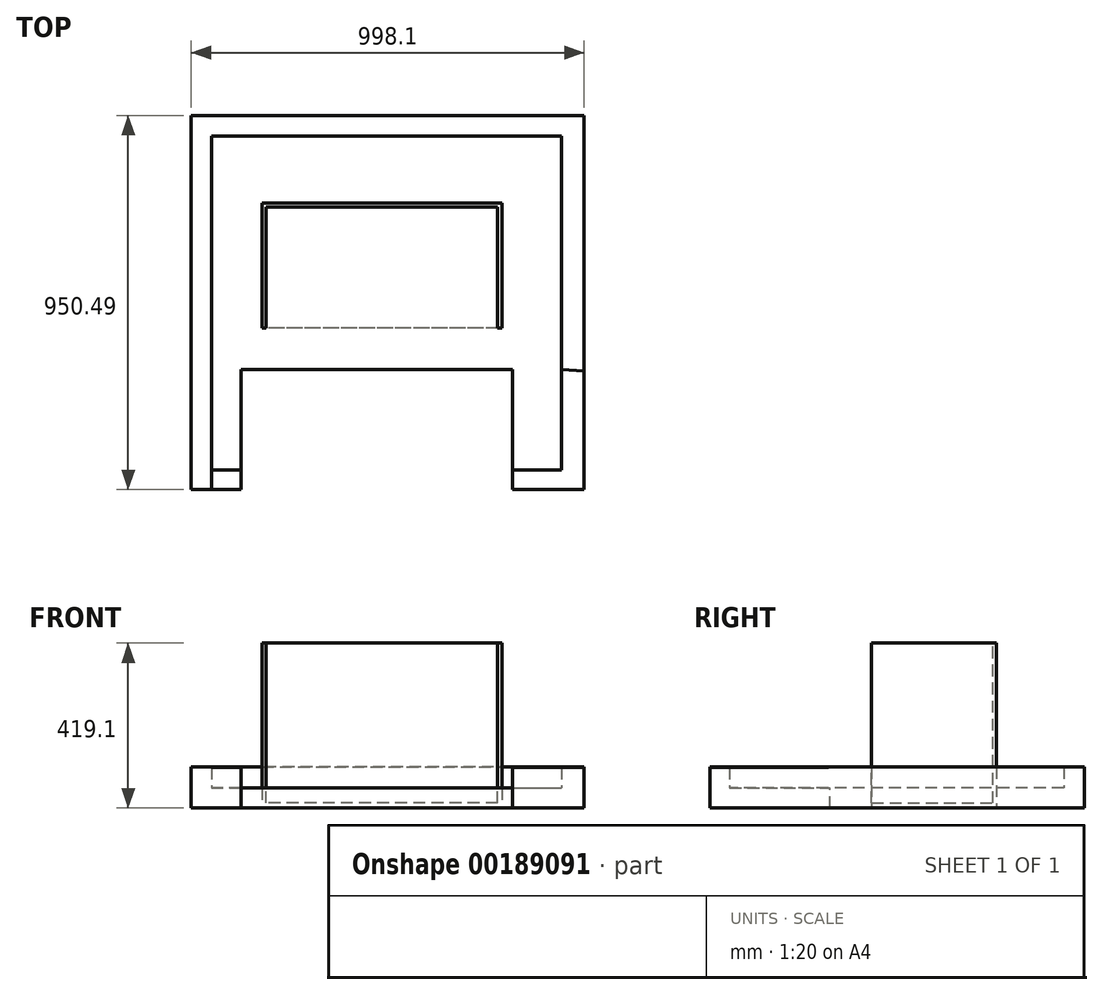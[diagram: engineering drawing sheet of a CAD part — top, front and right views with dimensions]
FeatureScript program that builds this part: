
annotation { "Feature Type Name" : "Feature", "Feature Type Description" : "" }
export const myFeature = defineFeature(function(context is Context, id is Id, definition is map)
    precondition{}
    {
        {
            var Q0;
            Q0=qCreatedBy(makeId("Top.planeOp"),FACE);
            var sketch = newSketch(context, id + "F0", { "sketchPlane" : qUnion([Q0])});
            skLineSegment(sketch, "E0.bottom", {"start": v(0, 0) * mm, "end": v(-609.6, 0) * mm});
            skLineSegment(sketch, "E0.top", {"start": v(0, -317.5) * mm, "end": v(-609.6, -317.5) * mm});
            skLineSegment(sketch, "E0.left", {"start": v(0, 0) * mm, "end": v(0, -317.5) * mm});
            skLineSegment(sketch, "E0.right", {"start": v(-609.6, 0) * mm, "end": v(-609.6, -317.5) * mm});
            skSolve(sketch);
        }
        {
            var Q0;
            Q0=makeQuery(id+"F0.imprint","IMPRINT",FACE,{"disambiguationData":[TD([[makeQuery(id+"F0.imprint","IMPRINT",EDGE,{"derivedFrom":sQuery(id+"F0.wireOp",EDGE,"E0.bottom")}),1.0]])]});
            extrude(context, id + "F1", {"entities" : qUnion([Q0]), "depth" : 419.1 * mm});
        }
        {
            var Q0;
            Q0=makeQuery(id+"F1.opExtrude","CAP_FACE",FACE,{"disambiguationData":[OSD([sQuery(id+"F0.wireOp",EDGE,"E0.bottom"),sQuery(id+"F0.wireOp",EDGE,"E0.top"),sQuery(id+"F0.wireOp",EDGE,"E0.left"),sQuery(id+"F0.wireOp",EDGE,"E0.right")])],"isStart":false});
            var sketch = newSketch(context, id + "F2", { "sketchPlane" : qUnion([Q0])});
            skLineSegment(sketch, "E1.bottom", {"start": v(-599.08, -317.5) * mm, "end": v(-10.7, -317.5) * mm});
            skLineSegment(sketch, "E1.top", {"start": v(-599.08, -9.65) * mm, "end": v(-10.7, -9.65) * mm});
            skLineSegment(sketch, "E1.left", {"start": v(-599.08, -317.5) * mm, "end": v(-599.08, -9.65) * mm});
            skLineSegment(sketch, "E1.right", {"start": v(-10.7, -317.5) * mm, "end": v(-10.7, -9.65) * mm});
            skSolve(sketch);
        }
        {
            var Q0;
            Q0=makeQuery(id+"F2.imprint","IMPRINT",FACE,{"disambiguationData":[TD([[makeQuery(id+"F2.imprint","IMPRINT",EDGE,{"derivedFrom":sQuery(id+"F2.wireOp",EDGE,"E1.bottom")}),-1.0]])]});
            extrude(context, id + "F3", {"entities" : qUnion([Q0]), "operationType" : NewBodyOperationType.REMOVE, "oppositeDirection" : true, "depth" : 406.4 * mm});
        }
        {
            var Q0;
            Q0=qCreatedBy(makeId("Top.planeOp"),FACE);
            var sketch = newSketch(context, id + "F4", { "sketchPlane" : qUnion([Q0])});
            skLineSegment(sketch, "E2.bottom", {"start": v(-737.99, 170.9) * mm, "end": v(151.01, 170.9) * mm});
            skLineSegment(sketch, "E2.top", {"start": v(-737.99, -423.02) * mm, "end": v(151.01, -423.02) * mm});
            skLineSegment(sketch, "E2.left", {"start": v(-737.99, 170.9) * mm, "end": v(-737.99, -423.02) * mm});
            skLineSegment(sketch, "E2.right", {"start": v(151.01, 170.9) * mm, "end": v(151.01, -423.02) * mm});
            skSolve(sketch);
        }
        {
            var Q0;
            Q0=makeQuery(id+"F4.imprint","IMPRINT",FACE,{"disambiguationData":[TD([[makeQuery(id+"F4.imprint","IMPRINT",EDGE,{"derivedFrom":sQuery(id+"F4.wireOp",EDGE,"E2.bottom")}),-1.0]])]});
            extrude(context, id + "F5", {"entities" : qUnion([Q0]), "depth" : 50.8 * mm});
        }
        {
            var Q0;
            Q0=makeQuery(id+"F5.opExtrude","CAP_FACE",FACE,{"disambiguationData":[OSD([sQuery(id+"F4.wireOp",EDGE,"E2.bottom"),sQuery(id+"F4.wireOp",EDGE,"E2.top"),sQuery(id+"F4.wireOp",EDGE,"E2.left"),sQuery(id+"F4.wireOp",EDGE,"E2.right")])],"isStart":true});
            var sketch = newSketch(context, id + "F6", { "sketchPlane" : qUnion([Q0])});
            skLineSegment(sketch, "E3.bottom", {"start": v(-737.99, 423.02) * mm, "end": v(-789.06, 423.02) * mm});
            skLineSegment(sketch, "E3.top", {"start": v(-737.99, -170.9) * mm, "end": v(-789.06, -170.9) * mm});
            skLineSegment(sketch, "E3.left", {"start": v(-737.99, 423.02) * mm, "end": v(-737.99, -170.9) * mm});
            skLineSegment(sketch, "E3.right", {"start": v(-789.06, 423.02) * mm, "end": v(-789.06, -170.9) * mm});
            skLineSegment(sketch, "E4.bottom", {"start": v(-789.06, 423.02) * mm, "end": v(151.01, 423.02) * mm});
            skLineSegment(sketch, "E4.top", {"start": v(-789.06, 500.05) * mm, "end": v(151.01, 500.05) * mm});
            skLineSegment(sketch, "E4.left", {"start": v(-789.06, 423.02) * mm, "end": v(-789.06, 500.05) * mm});
            skLineSegment(sketch, "E4.right", {"start": v(151.01, 423.02) * mm, "end": v(151.01, 500.05) * mm});
            skLineSegment(sketch, "E5.top", {"start": v(151.01, -170.9) * mm, "end": v(209.04, -170.9) * mm});
            skLineSegment(sketch, "E5.left", {"start": v(151.01, 500.05) * mm, "end": v(151.01, -170.9) * mm});
            skLineSegment(sketch, "E5.right", {"start": v(209.04, 426.81) * mm, "end": v(209.04, -170.9) * mm});
            skLineSegment(sketch, "E6.bottom", {"start": v(209.04, -170.9) * mm, "end": v(-789.06, -170.9) * mm});
            skLineSegment(sketch, "E6.top", {"start": v(209.04, -222.67) * mm, "end": v(-789.06, -222.67) * mm});
            skLineSegment(sketch, "E6.left", {"start": v(209.04, -170.9) * mm, "end": v(209.04, -222.67) * mm});
            skLineSegment(sketch, "E6.right", {"start": v(-789.06, -170.9) * mm, "end": v(-789.06, -222.67) * mm});
            skLineSegment(sketch, "E7", {"start": v(151.01, 423.02) * mm, "end": v(209.04, 426.81) * mm});
            skSolve(sketch);
        }
        {
            var Q0;
            {var subQ0=sQuery(id+"F6.wireOp",EDGE,"E3.left");Q0=makeQuery(id+"F6.imprint","IMPRINT",FACE,{"disambiguationData":[TD([[makeQuery(id+"F6.imprint","IMPRINT",EDGE,{"derivedFrom":subQ0}),1.0]])]});}
            var Q1;
            Q1=makeQuery(id+"F6.imprint","IMPRINT",FACE,{"disambiguationData":[TD([[makeQuery(id+"F6.imprint","IMPRINT",EDGE,{"derivedFrom":sQuery(id+"F6.wireOp",EDGE,"E6.top")}),-1.0]])]});
            var Q2;
            {var subQ5=sQuery(id+"F6.wireOp",EDGE,"E5.bottom");Q2=makeQuery(id+"F6.imprint","IMPRINT",FACE,{"disambiguationData":[TD([[makeQuery(id+"F6.imprint","IMPRINT",EDGE,{"derivedFrom":subQ5}),-1.0]])]});}
            var Q3;
            {var subQ4=sQuery(id+"F6.wireOp",EDGE,"E5.right");Q3=makeQuery(id+"F6.imprint","IMPRINT",FACE,{"disambiguationData":[TD([[makeQuery(id+"F6.imprint","IMPRINT",EDGE,{"derivedFrom":subQ4}),-1.0]])]});}
            extrude(context, id + "F7", {"entities" : qUnion([Q0, Q1, Q2, Q3]), "operationType" : NewBodyOperationType.ADD, "oppositeDirection" : true, "depth" : 104.14 * mm});
        }
        {
            var Q0;
            Q0=makeQuery(id+"F7.boolean.opBoolean","MERGE",FACE,{"derivedFrom":[makeQuery(id+"F5.opExtrude","SWEPT_FACE",FACE,{"disambiguationData":[OSD([sQuery(id+"F4.wireOp",EDGE,"E2.top")])]}),makeQuery(id+"F7.opExtrude","SWEPT_FACE",FACE,{"disambiguationData":[OSD([sQuery(id+"F6.wireOp",EDGE,"E4.bottom")])]})]});
            var sketch = newSketch(context, id + "F8", { "sketchPlane" : qUnion([Q0])});
            skLineSegment(sketch, "E8.bottom", {"start": v(-789.06, 0) * mm, "end": v(-662.47, 0) * mm});
            skLineSegment(sketch, "E8.top", {"start": v(-789.06, 50.8) * mm, "end": v(-662.47, 50.8) * mm});
            skLineSegment(sketch, "E8.left", {"start": v(-789.06, 0) * mm, "end": v(-789.06, 50.8) * mm});
            skLineSegment(sketch, "E8.right", {"start": v(-662.47, 0) * mm, "end": v(-662.47, 50.8) * mm});
            skLineSegment(sketch, "E9.bottom", {"start": v(-789.06, 104.14) * mm, "end": v(-737.99, 104.14) * mm});
            skLineSegment(sketch, "E9.top", {"start": v(-789.06, 50.8) * mm, "end": v(-737.99, 50.8) * mm});
            skLineSegment(sketch, "E9.left", {"start": v(-789.06, 104.14) * mm, "end": v(-789.06, 50.8) * mm});
            skLineSegment(sketch, "E9.right", {"start": v(-737.99, 104.14) * mm, "end": v(-737.99, 50.8) * mm});
            skLineSegment(sketch, "E10.bottom", {"start": v(151.01, 0) * mm, "end": v(27.1, 0) * mm});
            skLineSegment(sketch, "E10.top", {"start": v(151.01, 50.8) * mm, "end": v(27.1, 50.8) * mm});
            skLineSegment(sketch, "E10.left", {"start": v(151.01, 0) * mm, "end": v(151.01, 50.8) * mm});
            skLineSegment(sketch, "E10.right", {"start": v(27.1, 0) * mm, "end": v(27.1, 50.8) * mm});
            skLineSegment(sketch, "E11.bottom", {"start": v(151.01, 0) * mm, "end": v(209.04, 0) * mm});
            skLineSegment(sketch, "E11.top", {"start": v(151.01, 103.33) * mm, "end": v(209.04, 103.33) * mm});
            skLineSegment(sketch, "E11.left", {"start": v(151.01, 0) * mm, "end": v(151.01, 103.33) * mm});
            skLineSegment(sketch, "E11.right", {"start": v(209.04, 0) * mm, "end": v(209.04, 103.33) * mm});
            skSolve(sketch);
        }
        {
            var Q0;
            Q0 = qSketchRegion(id + "F8", true);
            extrude(context, id + "F9", {"entities" : qUnion([Q0]), "operationType" : NewBodyOperationType.ADD, "depth" : 304.8 * mm});
        }
        {
            var Q0;
            Q0=makeQuery(id+"F9.boolean.opBoolean","MERGE",FACE,{"derivedFrom":[makeQuery(id+"F5.opExtrude","CAP_FACE",FACE,{"disambiguationData":[OSD([sQuery(id+"F4.wireOp",EDGE,"E2.bottom"),sQuery(id+"F4.wireOp",EDGE,"E2.top"),sQuery(id+"F4.wireOp",EDGE,"E2.left"),sQuery(id+"F4.wireOp",EDGE,"E2.right")])],"isStart":false}),makeQuery(id+"F9.opExtrude","SWEPT_FACE",FACE,{"disambiguationData":[OSD([sQuery(id+"F8.wireOp",EDGE,"E8.top")])]}),makeQuery(id+"F9.opExtrude","SWEPT_FACE",FACE,{"disambiguationData":[OSD([sQuery(id+"F8.wireOp",EDGE,"E10.top")])]})]});
            var sketch = newSketch(context, id + "F10", { "sketchPlane" : qUnion([Q0])});
            skLineSegment(sketch, "E12.bottom", {"start": v(-662.47, -727.82) * mm, "end": v(-737.99, -727.82) * mm});
            skLineSegment(sketch, "E12.top", {"start": v(-662.47, -678.34) * mm, "end": v(-737.99, -678.34) * mm});
            skLineSegment(sketch, "E12.left", {"start": v(-662.47, -727.82) * mm, "end": v(-662.47, -678.34) * mm});
            skLineSegment(sketch, "E12.right", {"start": v(-737.99, -727.82) * mm, "end": v(-737.99, -678.34) * mm});
            skLineSegment(sketch, "E13.bottom", {"start": v(27.1, -727.82) * mm, "end": v(151.01, -727.82) * mm});
            skLineSegment(sketch, "E13.top", {"start": v(27.1, -678.34) * mm, "end": v(151.01, -678.34) * mm});
            skLineSegment(sketch, "E13.left", {"start": v(27.1, -727.82) * mm, "end": v(27.1, -678.34) * mm});
            skLineSegment(sketch, "E13.right", {"start": v(151.01, -727.82) * mm, "end": v(151.01, -678.34) * mm});
            skSolve(sketch);
        }
        {
            var Q0;
            Q0 = qSketchRegion(id + "F10", true);
            var Q1;
            Q1=makeQuery(id+"F9.opExtrude","SWEPT_FACE",FACE,{"disambiguationData":[OSD([sQuery(id+"F8.wireOp",EDGE,"E11.top")])]});
            extrude(context, id + "F11", {"entities" : qUnion([Q0]), "operationType" : NewBodyOperationType.ADD, "endBound" : BoundingType.UP_TO_SURFACE, "endBoundEntityFace" : qUnion([Q1]), "depth" : 50.8 * mm});
        }
    });
